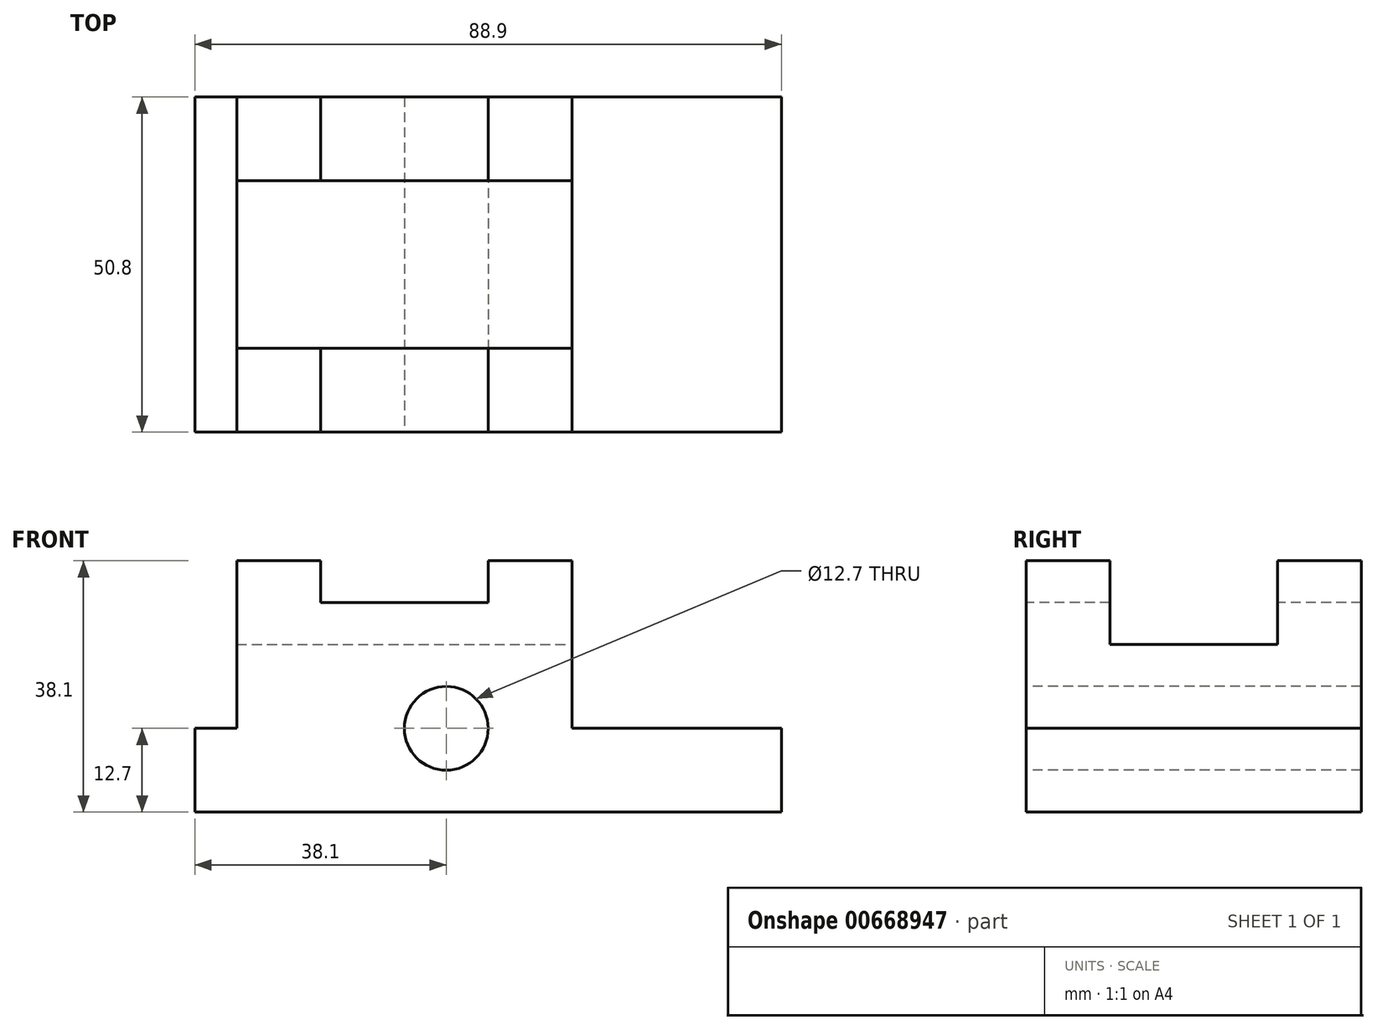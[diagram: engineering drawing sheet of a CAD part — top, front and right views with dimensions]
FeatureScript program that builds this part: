
annotation { "Feature Type Name" : "Feature", "Feature Type Description" : "" }
export const myFeature = defineFeature(function(context is Context, id is Id, definition is map)
    precondition{}
    {
        {
            var Q0;
            Q0=qCreatedBy(makeId("Front.planeOp"),FACE);
            var sketch = newSketch(context, id + "F0", { "sketchPlane" : qUnion([Q0])});
            skLineSegment(sketch, "E0.bottom", {"start": v(-44.45, 19.05) * mm, "end": v(44.45, 19.05) * mm});
            skLineSegment(sketch, "E0.top", {"start": v(-44.45, -19.05) * mm, "end": v(44.45, -19.05) * mm});
            skLineSegment(sketch, "E0.left", {"start": v(-44.45, 19.05) * mm, "end": v(-44.45, -19.05) * mm});
            skLineSegment(sketch, "E0.right", {"start": v(44.45, 19.05) * mm, "end": v(44.45, -19.05) * mm});
            skPoint(sketch, "E0.middle", {"position": v(0, 0) * mm});
            skSolve(sketch);
        }
        {
            var Q0;
            Q0=makeQuery(id+"F0.imprint","IMPRINT",FACE,{"disambiguationData":[TD([[makeQuery(id+"F0.imprint","IMPRINT",EDGE,{"derivedFrom":sQuery(id+"F0.wireOp",EDGE,"E0.bottom")}),-1.0]])]});
            extrude(context, id + "F1", {"entities" : qUnion([Q0]), "depth" : 50.8 * mm, "offsetDistance" : 25.4 * mm});
        }
        {
            var Q0;
            Q0=makeQuery(id+"F1.opExtrude","CAP_FACE",FACE,{"disambiguationData":[OSD([sQuery(id+"F0.wireOp",EDGE,"E0.bottom"),sQuery(id+"F0.wireOp",EDGE,"E0.top"),sQuery(id+"F0.wireOp",EDGE,"E0.left"),sQuery(id+"F0.wireOp",EDGE,"E0.right")])],"isStart":false});
            var sketch = newSketch(context, id + "F2", { "sketchPlane" : qUnion([Q0])});
            skLineSegment(sketch, "E1.bottom", {"start": v(12.7, 19.05) * mm, "end": v(44.45, 19.05) * mm});
            skLineSegment(sketch, "E1.top", {"start": v(12.7, -6.35) * mm, "end": v(44.45, -6.35) * mm});
            skLineSegment(sketch, "E1.left", {"start": v(12.7, 19.05) * mm, "end": v(12.7, -6.35) * mm});
            skLineSegment(sketch, "E1.right", {"start": v(44.45, 19.05) * mm, "end": v(44.45, -6.35) * mm});
            skSolve(sketch);
        }
        {
            var Q0;
            Q0=makeQuery(id+"F2.imprint","IMPRINT",FACE,{"disambiguationData":[TD([[makeQuery(id+"F2.imprint","IMPRINT",EDGE,{"derivedFrom":sQuery(id+"F2.wireOp",EDGE,"E1.bottom")}),-1.0]])]});
            extrude(context, id + "F3", {"entities" : qUnion([Q0]), "operationType" : NewBodyOperationType.REMOVE, "oppositeDirection" : true, "depth" : 50.8 * mm, "offsetDistance" : 25.4 * mm});
        }
        {
            var Q0;
            Q0=makeQuery(id+"F1.opExtrude","CAP_FACE",FACE,{"disambiguationData":[OSD([sQuery(id+"F0.wireOp",EDGE,"E0.bottom"),sQuery(id+"F0.wireOp",EDGE,"E0.top"),sQuery(id+"F0.wireOp",EDGE,"E0.left"),sQuery(id+"F0.wireOp",EDGE,"E0.right")])],"isStart":false});
            var sketch = newSketch(context, id + "F4", { "sketchPlane" : qUnion([Q0])});
            skLineSegment(sketch, "E2.bottom", {"start": v(-25.4, 19.05) * mm, "end": v(0, 19.05) * mm});
            skLineSegment(sketch, "E2.top", {"start": v(-25.4, 12.7) * mm, "end": v(0, 12.7) * mm});
            skLineSegment(sketch, "E2.left", {"start": v(-25.4, 19.05) * mm, "end": v(-25.4, 12.7) * mm});
            skLineSegment(sketch, "E2.right", {"start": v(0, 19.05) * mm, "end": v(0, 12.7) * mm});
            skSolve(sketch);
        }
        {
            var Q0;
            Q0=makeQuery(id+"F4.imprint","IMPRINT",FACE,{"disambiguationData":[TD([[makeQuery(id+"F4.imprint","IMPRINT",EDGE,{"derivedFrom":sQuery(id+"F4.wireOp",EDGE,"E2.bottom")}),-1.0]])]});
            extrude(context, id + "F5", {"entities" : qUnion([Q0]), "operationType" : NewBodyOperationType.REMOVE, "oppositeDirection" : true, "depth" : 50.8 * mm, "offsetDistance" : 25.4 * mm});
        }
        {
            var Q0;
            Q0=makeQuery(id+"F1.opExtrude","CAP_FACE",FACE,{"disambiguationData":[OSD([sQuery(id+"F0.wireOp",EDGE,"E0.bottom"),sQuery(id+"F0.wireOp",EDGE,"E0.top"),sQuery(id+"F0.wireOp",EDGE,"E0.left"),sQuery(id+"F0.wireOp",EDGE,"E0.right")])],"isStart":false});
            var sketch = newSketch(context, id + "F6", { "sketchPlane" : qUnion([Q0])});
            skLineSegment(sketch, "E3.bottom", {"start": v(-38.1, 19.05) * mm, "end": v(-44.45, 19.05) * mm});
            skLineSegment(sketch, "E3.top", {"start": v(-38.1, -6.35) * mm, "end": v(-44.45, -6.35) * mm});
            skLineSegment(sketch, "E3.left", {"start": v(-38.1, 19.05) * mm, "end": v(-38.1, -6.35) * mm});
            skLineSegment(sketch, "E3.right", {"start": v(-44.45, 19.05) * mm, "end": v(-44.45, -6.35) * mm});
            skSolve(sketch);
        }
        {
            var Q0;
            Q0=makeQuery(id+"F6.imprint","IMPRINT",FACE,{"disambiguationData":[TD([[makeQuery(id+"F6.imprint","IMPRINT",EDGE,{"derivedFrom":sQuery(id+"F6.wireOp",EDGE,"E3.bottom")}),-1.0]])]});
            extrude(context, id + "F7", {"entities" : qUnion([Q0]), "operationType" : NewBodyOperationType.REMOVE, "oppositeDirection" : true, "depth" : 50.8 * mm, "offsetDistance" : 25.4 * mm});
        }
        {
            var Q0;
            Q0=makeQuery(id+"F3.boolean.opBoolean","COPY",FACE,{"derivedFrom":makeQuery(id+"F3.opExtrude","SWEPT_FACE",FACE,{"disambiguationData":[OSD([sQuery(id+"F2.wireOp",EDGE,"E1.left")])]})});
            var sketch = newSketch(context, id + "F8", { "sketchPlane" : qUnion([Q0])});
            skLineSegment(sketch, "E4.bottom", {"start": v(-38.1, 19.05) * mm, "end": v(-12.7, 19.05) * mm});
            skLineSegment(sketch, "E4.top", {"start": v(-38.1, 6.35) * mm, "end": v(-12.7, 6.35) * mm});
            skLineSegment(sketch, "E4.left", {"start": v(-38.1, 19.05) * mm, "end": v(-38.1, 6.35) * mm});
            skLineSegment(sketch, "E4.right", {"start": v(-12.7, 19.05) * mm, "end": v(-12.7, 6.35) * mm});
            skSolve(sketch);
        }
        {
            var Q0;
            Q0=makeQuery(id+"F8.imprint","IMPRINT",FACE,{"disambiguationData":[TD([[makeQuery(id+"F8.imprint","IMPRINT",EDGE,{"derivedFrom":sQuery(id+"F8.wireOp",EDGE,"E4.bottom")}),1.0]])]});
            extrude(context, id + "F9", {"entities" : qUnion([Q0]), "operationType" : NewBodyOperationType.REMOVE, "oppositeDirection" : true, "depth" : 50.8 * mm, "offsetDistance" : 25.4 * mm});
        }
        {
            var Q0;
            Q0=makeQuery(id+"F1.opExtrude","CAP_FACE",FACE,{"disambiguationData":[OSD([sQuery(id+"F0.wireOp",EDGE,"E0.bottom"),sQuery(id+"F0.wireOp",EDGE,"E0.top"),sQuery(id+"F0.wireOp",EDGE,"E0.left"),sQuery(id+"F0.wireOp",EDGE,"E0.right")])],"isStart":false});
            var sketch = newSketch(context, id + "F10", { "sketchPlane" : qUnion([Q0])});
            skCircle(sketch, "E5", {"center": v(-6.35, -6.35) * mm, "radius": 6.35 * mm});
            skSolve(sketch);
        }
        {
            var Q0;
            Q0=makeQuery(id+"F10.imprint","IMPRINT",FACE,{"disambiguationData":[TD([[makeQuery(id+"F10.imprint","IMPRINT",EDGE,{"derivedFrom":sQuery(id+"F10.wireOp",EDGE,"E5")}),1.0]])]});
            extrude(context, id + "F11", {"entities" : qUnion([Q0]), "operationType" : NewBodyOperationType.REMOVE, "oppositeDirection" : true, "depth" : 50.8 * mm, "offsetDistance" : 25.4 * mm});
        }
    });
